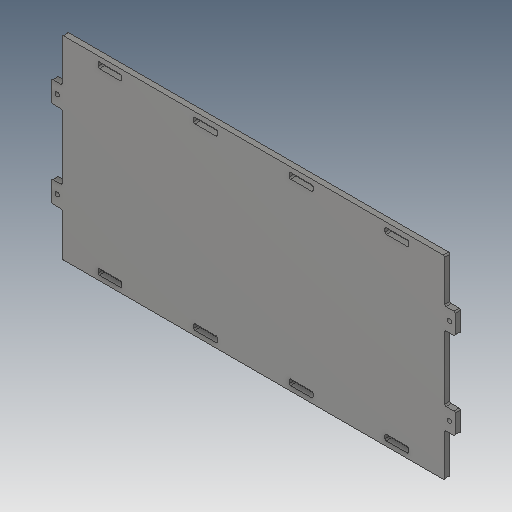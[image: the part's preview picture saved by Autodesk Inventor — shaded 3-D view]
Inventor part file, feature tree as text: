
AUTODESK INVENTOR PART (.ipt)
format: ipt  version: 2023.5 (Build 275446000, 446)  size: 168,960 bytes
history: native  units: in
note: dims shown in document units (in); Inventor stores cm internally (conversion verified against a paired STEP export)
features: fillet x1
ambient origin geometry x8: Origin, YZ Plane, XZ Plane, XY Plane, X Axis, Y Axis, Z Axis, Center Point
bodies: Solid1 (feature_tree)
feature tree (1):
  fillet  "Fillet3"  [1 undecoded]
note: 1 required parameter value undecoded (feature->parameter linkage not recoverable at this tier; creation-order binding heuristic only, values carry confidence <= 0.55)
